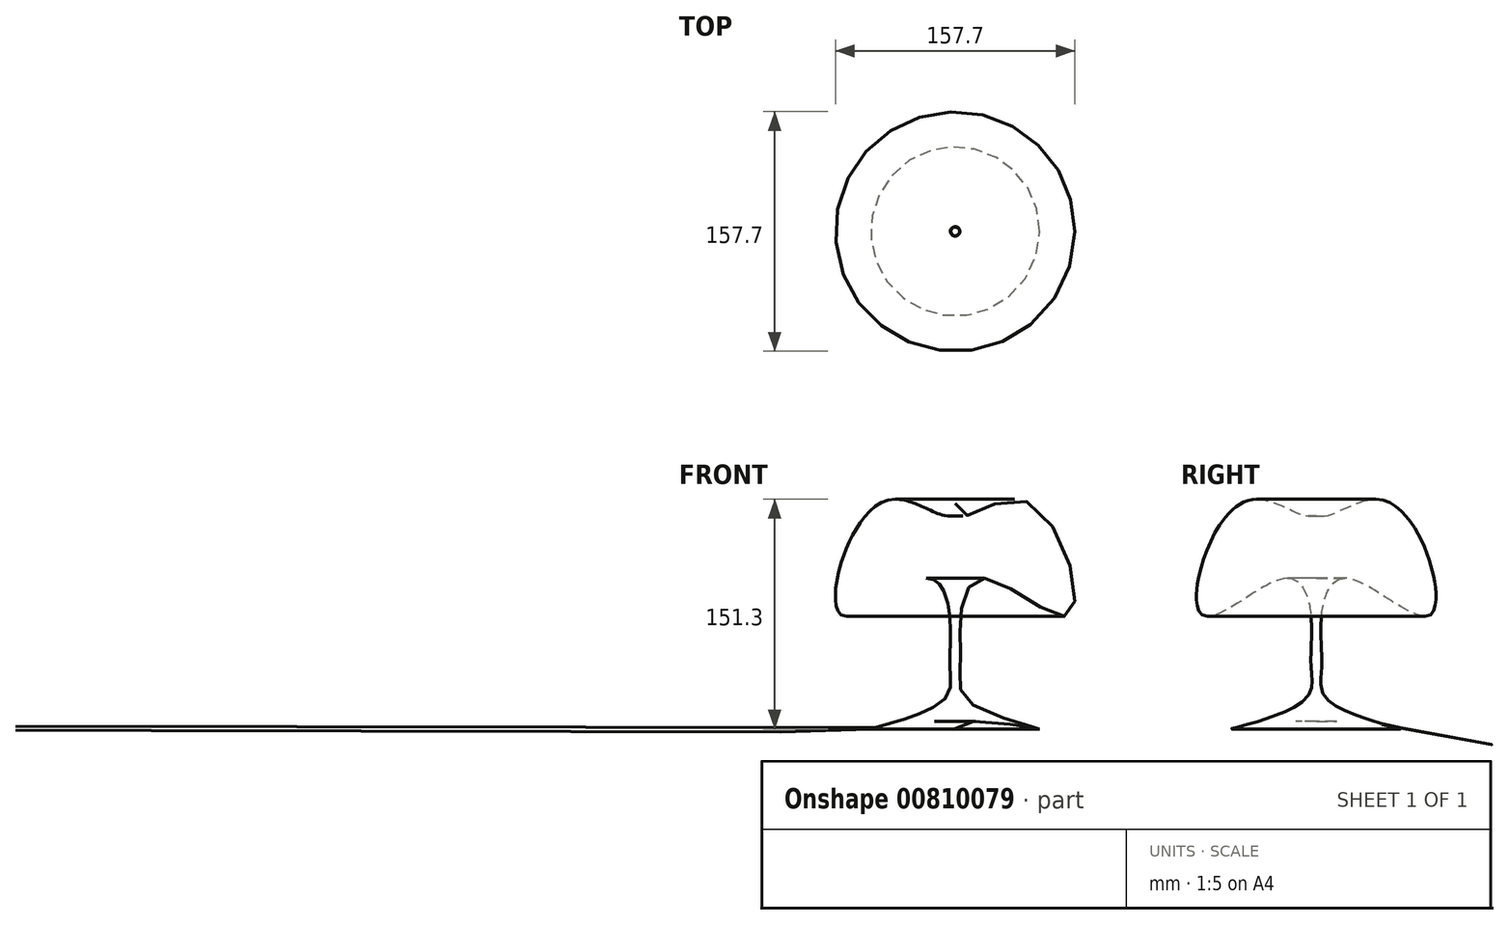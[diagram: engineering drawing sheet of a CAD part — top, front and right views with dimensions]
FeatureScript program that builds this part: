
annotation { "Feature Type Name" : "Feature", "Feature Type Description" : "" }
export const myFeature = defineFeature(function(context is Context, id is Id, definition is map)
    precondition{}
    {
        {
            var Q0;
            Q0=qCreatedBy(makeId("Front.planeOp"),FACE);
            var sketch = newSketch(context, id + "F0", { "sketchPlane" : qUnion([Q0])});
            skLineSegment(sketch, "E0", {"start": v(0, 72.95) * mm, "end": v(0, -72.35) * mm});
            skFitSpline(sketch, "E1", {"points": [v(0, 72.95) * mm, v(42.4, 75.52) * mm, v(75.57, 0) * mm, v(20.15, 23.66) * mm, v(3.63, 0) * mm, v(3.47, -35.47) * mm, v(9.9, -58.43) * mm, v(55.26, -75.5) * mm, v(0, -75.2) * mm], "startDerivative": vector(0, -523.28) * mm, "endDerivative": vector(0, -225.86) * mm});
            skSolve(sketch);
        }
        {
            var Q0;
            Q0=sQuery(id+"F0.wireOp",EDGE,"E1");
            var Q1;
            Q1=sQuery(id+"F0.wireOp",EDGE,"E0");
            revolve(context, id + "F1", {"bodyType" : ToolBodyType.SURFACE, "surfaceOperationType" : NewSurfaceOperationType.NEW, "surfaceEntities" : qUnion([Q0]), "axis" : qUnion([Q1]), "revolveType" : RevolveType.FULL});
        }
    });
